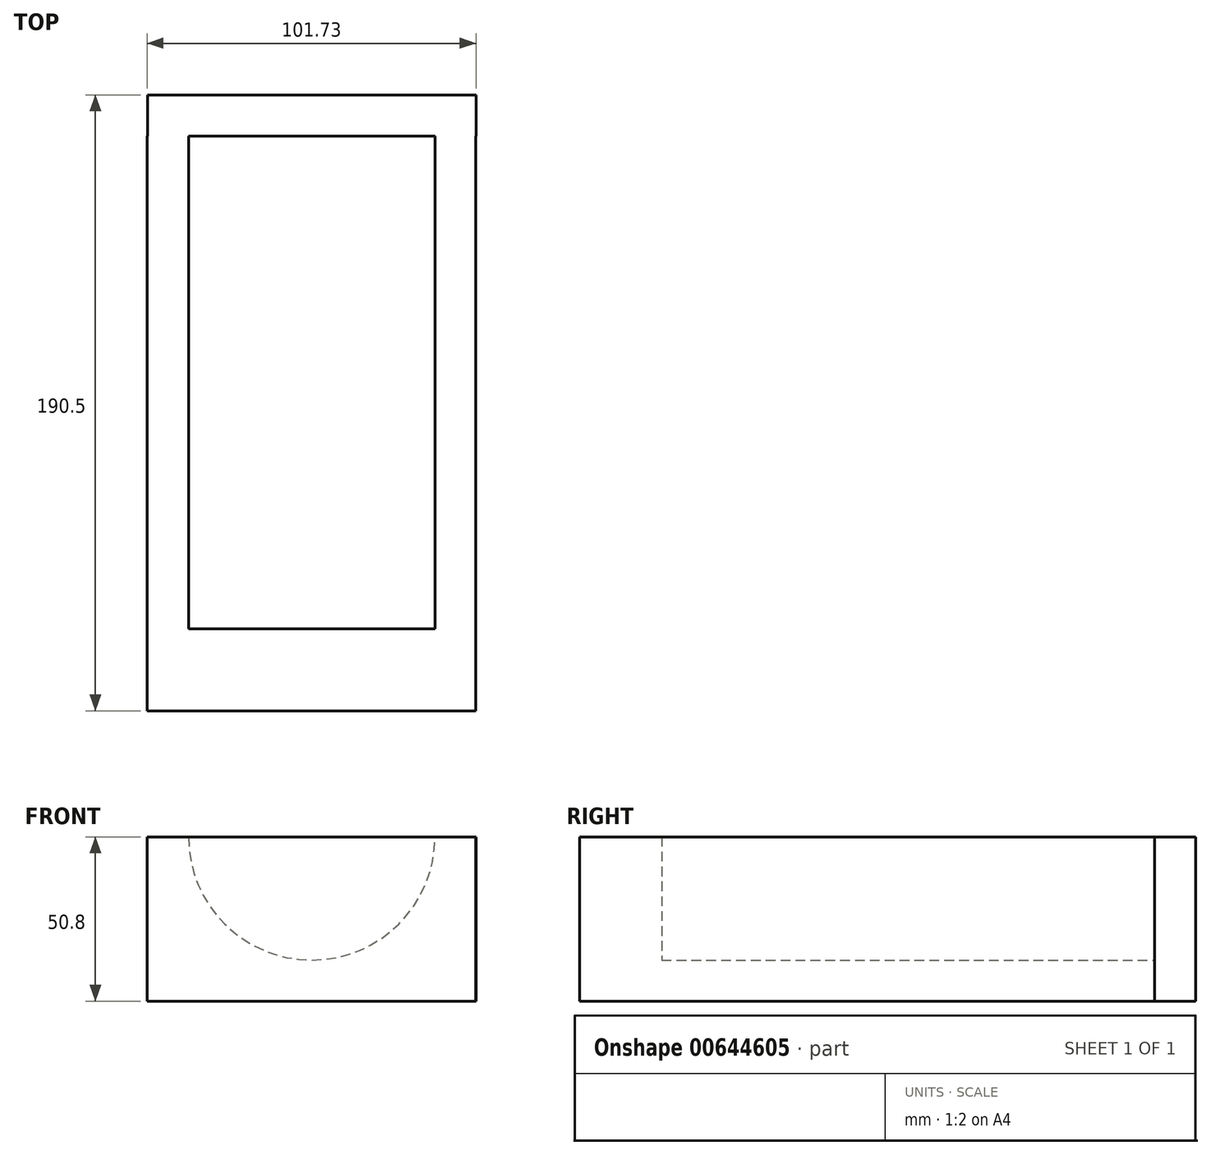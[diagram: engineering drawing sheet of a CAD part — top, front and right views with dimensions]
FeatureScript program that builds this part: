
annotation { "Feature Type Name" : "Feature", "Feature Type Description" : "" }
export const myFeature = defineFeature(function(context is Context, id is Id, definition is map)
    precondition{}
    {
        {
            var Q0;
            Q0=qCreatedBy(makeId("Front.planeOp"),FACE);
            var sketch = newSketch(context, id + "F0", { "sketchPlane" : qUnion([Q0])});
            skLineSegment(sketch, "E0.bottom", {"start": v(-50.93, 0) * mm, "end": v(50.67, 0) * mm});
            skLineSegment(sketch, "E0.top", {"start": v(-50.93, -50.8) * mm, "end": v(50.67, -50.8) * mm});
            skLineSegment(sketch, "E0.left", {"start": v(-50.93, 0) * mm, "end": v(-50.93, -50.8) * mm});
            skLineSegment(sketch, "E0.right", {"start": v(50.67, 0) * mm, "end": v(50.67, -50.8) * mm});
            skSolve(sketch);
        }
        {
            var Q0;
            Q0 = qSketchRegion(id + "F0", true);
            extrude(context, id + "F1", {"entities" : qUnion([Q0]), "depth" : 177.8 * mm, "offsetDistance" : 25.4 * mm});
        }
        {
            var Q0;
            Q0=makeQuery(id+"F1.opExtrude","CAP_FACE",FACE,{"disambiguationData":[OSD([sQuery(id+"F0.wireOp",EDGE,"E0.bottom"),sQuery(id+"F0.wireOp",EDGE,"E0.top"),sQuery(id+"F0.wireOp",EDGE,"E0.left"),sQuery(id+"F0.wireOp",EDGE,"E0.right")])],"isStart":true});
            var sketch = newSketch(context, id + "F2", { "sketchPlane" : qUnion([Q0])});
            skLineSegment(sketch, "E1", {"start": v(0, 0) * mm, "end": v(38.1, 0) * mm});
            skSolve(sketch);
        }
        {
            var Q0;
            Q0=qCreatedBy(makeId("Front.planeOp"),FACE);
            var sketch = newSketch(context, id + "F3", { "sketchPlane" : qUnion([Q0])});
            skLineSegment(sketch, "E2", {"start": v(0, 0) * mm, "end": v(38.1, 0) * mm});
            skLineSegment(sketch, "E3", {"start": v(0, 0) * mm, "end": v(-38.1, 0) * mm});
            skLineSegment(sketch, "E4", {"start": v(0, 0) * mm, "end": v(0, -38.1) * mm});
            skArc(sketch, "E5", {"start": v(-38.1, 0) * mm, "mid": v(0, -38.1) * mm, "end": v(38.1, 0) * mm});
            skSolve(sketch);
        }
        {
            var Q0;
            {var subQ0=sQuery(id+"F3.wireOp",EDGE,"E3");Q0=makeQuery(id+"F3.imprint","IMPRINT",FACE,{"disambiguationData":[TD([[makeQuery(id+"F3.imprint","IMPRINT",EDGE,{"derivedFrom":subQ0}),1.0]])]});}
            var Q1;
            {var subQ0=sQuery(id+"F3.wireOp",EDGE,"E2");Q1=makeQuery(id+"F3.imprint","IMPRINT",FACE,{"disambiguationData":[TD([[makeQuery(id+"F3.imprint","IMPRINT",EDGE,{"derivedFrom":subQ0}),-1.0]])]});}
            extrude(context, id + "F4", {"entities" : qUnion([Q0, Q1]), "operationType" : NewBodyOperationType.REMOVE, "depth" : 152.4 * mm, "offsetDistance" : 25.4 * mm});
        }
        {
            var Q0;
            {var subQ2=sQuery(id+"F2.wireOp",EDGE,"E1");Q0=makeQuery(id+"F2.imprint","IMPRINT",FACE,{"disambiguationData":[TD([[makeQuery(id+"F2.imprint","IMPRINT",EDGE,{"derivedFrom":subQ2}),1.0]])]});}
            var sketch = newSketch(context, id + "F5", { "sketchPlane" : qUnion([Q0])});
            skLineSegment(sketch, "E6.bottom", {"start": v(-50.67, 0) * mm, "end": v(50.93, 0) * mm});
            skLineSegment(sketch, "E6.top", {"start": v(-50.67, -50.8) * mm, "end": v(50.93, -50.8) * mm});
            skLineSegment(sketch, "E6.left", {"start": v(-50.67, 0) * mm, "end": v(-50.67, -50.8) * mm});
            skLineSegment(sketch, "E6.right", {"start": v(50.93, 0) * mm, "end": v(50.93, -50.8) * mm});
            skLineSegment(sketch, "E7", {"start": v(0, 0) * mm, "end": v(-44.45, 0) * mm});
            skLineSegment(sketch, "E8", {"start": v(0, 0) * mm, "end": v(44.45, 0) * mm});
            skLineSegment(sketch, "E9", {"start": v(0, 0) * mm, "end": v(0, -44.45) * mm});
            skArc(sketch, "E10", {"start": v(-44.45, 0) * mm, "mid": v(0, -44.45) * mm, "end": v(44.45, 0) * mm});
            skLineSegment(sketch, "E11", {"start": v(0, 0) * mm, "end": v(-38.1, 0) * mm});
            skLineSegment(sketch, "E12", {"start": v(0, 0) * mm, "end": v(38.1, 0) * mm});
            skLineSegment(sketch, "E13", {"start": v(0, 0) * mm, "end": v(0, -38.1) * mm});
            skArc(sketch, "E14", {"start": v(-38.1, 0) * mm, "mid": v(0, -38.1) * mm, "end": v(38.1, 0) * mm});
            skLineSegment(sketch, "E15", {"start": v(-38.1, 0) * mm, "end": v(-44.45, 0) * mm});
            skLineSegment(sketch, "E16", {"start": v(44.45, 0) * mm, "end": v(38.1, 0) * mm});
            skSolve(sketch);
        }
        {
            var Q0;
            {var subQ0=sQuery(id+"F5.wireOp",EDGE,"E9");Q0=makeQuery(id+"F5.imprint","IMPRINT",FACE,{"disambiguationData":[TD([[makeQuery(id+"F5.imprint","IMPRINT",EDGE,{"derivedFrom":subQ0}),1.0]])]});}
            var Q1;
            {var subQ0=sQuery(id+"F5.wireOp",EDGE,"E9");Q1=makeQuery(id+"F5.imprint","IMPRINT",FACE,{"disambiguationData":[TD([[makeQuery(id+"F5.imprint","IMPRINT",EDGE,{"derivedFrom":subQ0}),-1.0]])]});}
            extrude(context, id + "F6", {"entities" : qUnion([Q0, Q1]), "operationType" : NewBodyOperationType.REMOVE, "oppositeDirection" : true, "depth" : 3.8 * mm, "offsetDistance" : 25.4 * mm});
        }
        {
            var Q0;
            {var subQ2=sQuery(id+"F2.wireOp",EDGE,"E1");Q0=makeQuery(id+"F2.imprint","IMPRINT",FACE,{"disambiguationData":[TD([[makeQuery(id+"F2.imprint","IMPRINT",EDGE,{"derivedFrom":subQ2}),1.0]])]});}
            var sketch = newSketch(context, id + "F7", { "sketchPlane" : qUnion([Q0])});
            skLineSegment(sketch, "E17", {"start": v(0, 0) * mm, "end": v(-50.8, 0) * mm});
            skLineSegment(sketch, "E18", {"start": v(0, 0) * mm, "end": v(50.8, 0) * mm});
            skLineSegment(sketch, "E19", {"start": v(50.8, 0) * mm, "end": v(50.8, -50.8) * mm});
            skLineSegment(sketch, "E20.bottom", {"start": v(-50.8, 0) * mm, "end": v(50.8, 0) * mm});
            skLineSegment(sketch, "E20.top", {"start": v(-50.8, -50.8) * mm, "end": v(50.8, -50.8) * mm});
            skLineSegment(sketch, "E20.left", {"start": v(-50.8, 0) * mm, "end": v(-50.8, -50.8) * mm});
            skSolve(sketch);
        }
        {
            var Q0;
            Q0 = qSketchRegion(id + "F7", true);
            extrude(context, id + "F8", {"entities" : qUnion([Q0]), "operationType" : NewBodyOperationType.ADD, "depth" : 12.7 * mm, "offsetDistance" : 25.4 * mm});
        }
    });
